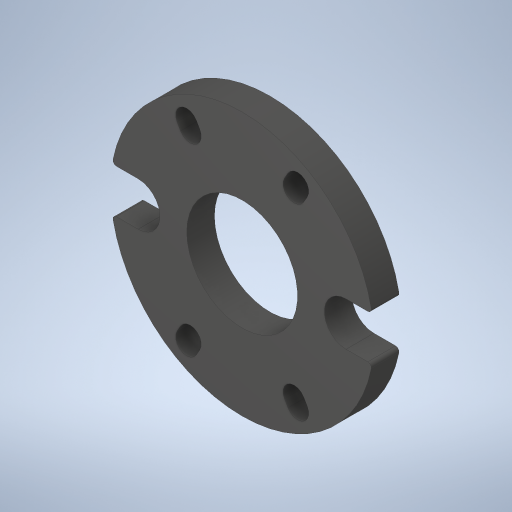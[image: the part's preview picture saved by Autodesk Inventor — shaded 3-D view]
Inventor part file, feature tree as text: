
AUTODESK INVENTOR PART (.ipt)
format: ipt  version: 2023.4 (Build 274418000, 418)  size: 273,408 bytes
history: native  units: in
note: dims shown in document units (in); Inventor stores cm internally (conversion verified against a paired STEP export)
features: fillet x1
ambient origin geometry x8: Origin, YZ Plane, XZ Plane, XY Plane, X Axis, Y Axis, Z Axis, Center Point
bodies: Solid1 (feature_tree)
feature tree (1):
  fillet  "Fillet1"  [1 undecoded]
note: 1 required parameter value undecoded (feature->parameter linkage not recoverable at this tier; creation-order binding heuristic only, values carry confidence <= 0.55)
